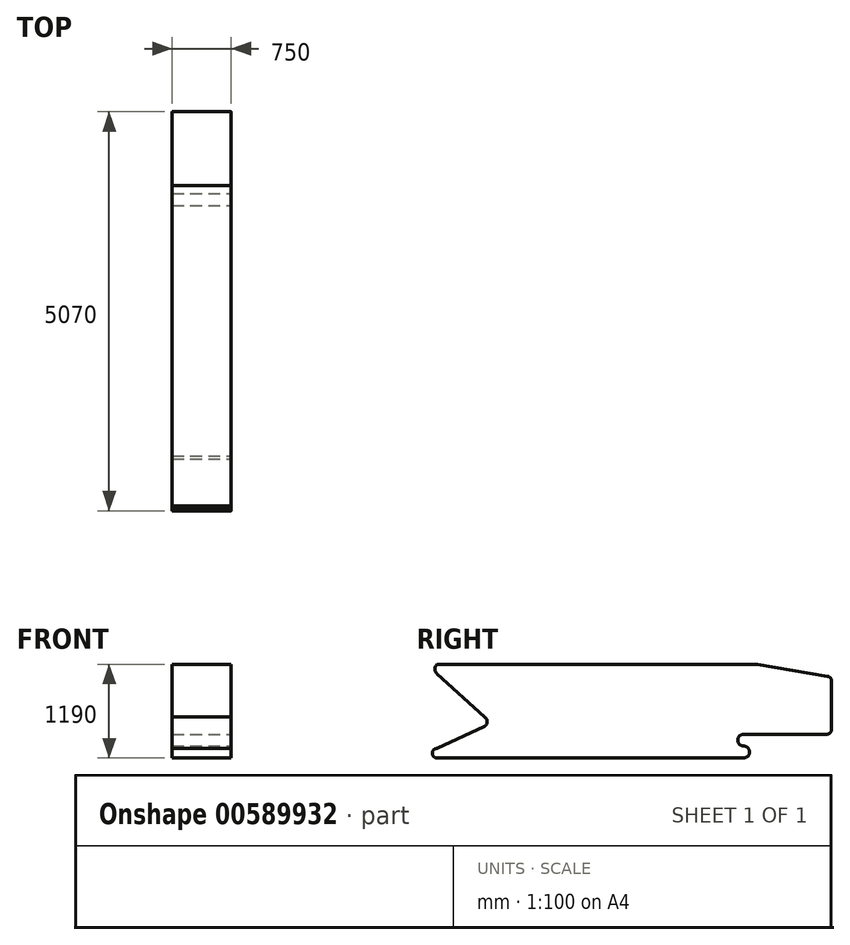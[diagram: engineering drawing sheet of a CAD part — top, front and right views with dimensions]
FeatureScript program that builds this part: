
annotation { "Feature Type Name" : "Feature", "Feature Type Description" : "" }
export const myFeature = defineFeature(function(context is Context, id is Id, definition is map)
    precondition{}
    {
        {
            var Q0;
            Q0=qCreatedBy(makeId("Right.planeOp"),FACE);
            var sketch = newSketch(context, id + "F0", { "sketchPlane" : qUnion([Q0])});
            skLineSegment(sketch, "E0", {"start": v(0, 0) * mm, "end": v(3895, 0) * mm});
            skArc(sketch, "E1", {"start": v(3895, 0) * mm, "mid": v(3970, 75) * mm, "end": v(3895, 150) * mm});
            skArc(sketch, "E2", {"start": v(3895, 150) * mm, "mid": v(3820, 225) * mm, "end": v(3895, 300) * mm});
            skLineSegment(sketch, "E3", {"start": v(3895, 300) * mm, "end": v(4950, 300) * mm});
            skLineSegment(sketch, "E4", {"start": v(5010, 360) * mm, "end": v(5010, 979.33) * mm});
            skPoint(sketch, "E5.visualSharp", {"position": v(5010, 300) * mm});
            skArc(sketch, "E5.filletArc", {"start": v(4950, 300) * mm, "mid": v(4992.43, 317.57) * mm, "end": v(5010, 360) * mm});
            skLineSegment(sketch, "E6", {"start": v(4960.05, 1038.49) * mm, "end": v(4068.1, 1190) * mm});
            skArc(sketch, "E7", {"start": v(0, 0) * mm, "mid": v(-60, 60) * mm, "end": v(0, 120) * mm});
            skLineSegment(sketch, "E8", {"start": v(0, 120) * mm, "end": v(600, 400) * mm});
            skArc(sketch, "E9", {"start": v(600, 400) * mm, "mid": v(638.21, 460) * mm, "end": v(600, 520) * mm});
            skLineSegment(sketch, "E10", {"start": v(600, 520) * mm, "end": v(0, 1070) * mm});
            skArc(sketch, "E11", {"start": v(0, 1070) * mm, "mid": v(-26.4, 1130) * mm, "end": v(0, 1190) * mm});
            skLineSegment(sketch, "E12", {"start": v(0, 1190) * mm, "end": v(4068.1, 1190) * mm});
            skPoint(sketch, "E13.visualSharp", {"position": v(5010, 1030) * mm});
            skArc(sketch, "E13.filletArc", {"start": v(5010, 979.33) * mm, "mid": v(4995.84, 1018.04) * mm, "end": v(4960.05, 1038.49) * mm});
            skSolve(sketch);
        }
        {
            var Q0;
            Q0=sQuery(id+"F0.wireOp",EDGE,"E10");
            var Q1;
            Q1=sQuery(id+"F0.wireOp",EDGE,"E11");
            var Q2;
            Q2=sQuery(id+"F0.wireOp",EDGE,"E12");
            var Q3;
            Q3=sQuery(id+"F0.wireOp",EDGE,"E6");
            var Q4;
            Q4=sQuery(id+"F0.wireOp",EDGE,"E13.filletArc");
            var Q5;
            Q5=sQuery(id+"F0.wireOp",EDGE,"E4");
            var Q6;
            Q6=sQuery(id+"F0.wireOp",EDGE,"E5.filletArc");
            var Q7;
            Q7=sQuery(id+"F0.wireOp",EDGE,"E3");
            var Q8;
            Q8=sQuery(id+"F0.wireOp",EDGE,"E2");
            var Q9;
            Q9=sQuery(id+"F0.wireOp",EDGE,"E1");
            var Q10;
            Q10=sQuery(id+"F0.wireOp",EDGE,"E0");
            var Q11;
            Q11=sQuery(id+"F0.wireOp",EDGE,"E7");
            var Q12;
            Q12=sQuery(id+"F0.wireOp",EDGE,"E8");
            var Q13;
            Q13=sQuery(id+"F0.wireOp",EDGE,"E9");
            extrude(context, id + "F1", {"bodyType" : ToolBodyType.SURFACE, "surfaceEntities" : qUnion([Q0, Q1, Q2, Q3, Q4, Q5, Q6, Q7, Q8, Q9, Q10, Q11, Q12, Q13]), "depth" : 750 * mm, "offsetDistance" : 25 * mm});
        }
    });
